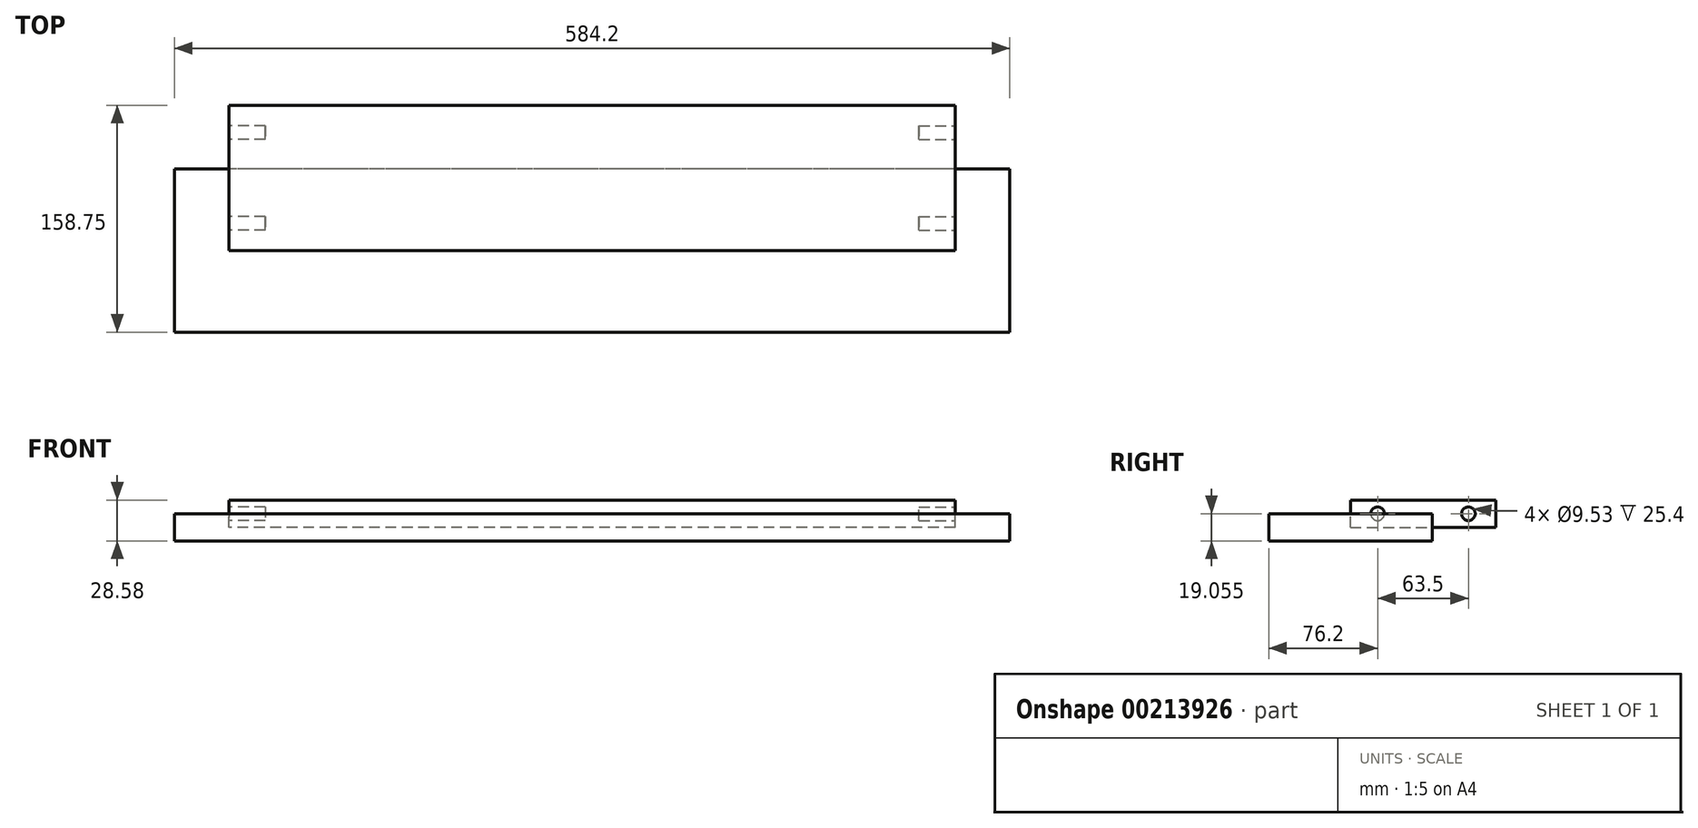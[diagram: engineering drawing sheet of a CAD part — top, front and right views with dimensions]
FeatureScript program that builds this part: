
annotation { "Feature Type Name" : "Feature", "Feature Type Description" : "" }
export const myFeature = defineFeature(function(context is Context, id is Id, definition is map)
    precondition{}
    {
        {
            var Q0;
            Q0=qCreatedBy(makeId("Right.planeOp"),FACE);
            var sketch = newSketch(context, id + "F0", { "sketchPlane" : qUnion([Q0])});
            skLineSegment(sketch, "E0.bottom", {"start": v(0, 0) * mm, "end": v(101.6, 0) * mm});
            skLineSegment(sketch, "E0.top", {"start": v(0, 19.05) * mm, "end": v(101.6, 19.05) * mm});
            skLineSegment(sketch, "E0.left", {"start": v(0, 0) * mm, "end": v(0, 19.05) * mm});
            skLineSegment(sketch, "E0.right", {"start": v(101.6, 0) * mm, "end": v(101.6, 19.05) * mm});
            skSolve(sketch);
        }
        {
            var Q0;
            Q0 = qSketchRegion(id + "F0", true);
            extrude(context, id + "F1", {"entities" : qUnion([Q0]), "endBound" : BoundingType.SYMMETRIC, "depth" : 508 * mm});
        }
        {
            var Q0;
            Q0=makeQuery(id+"F1.opExtrude","CAP_FACE",FACE,{"disambiguationData":[OSD([sQuery(id+"F0.wireOp",EDGE,"E0.bottom"),sQuery(id+"F0.wireOp",EDGE,"E0.top"),sQuery(id+"F0.wireOp",EDGE,"E0.left"),sQuery(id+"F0.wireOp",EDGE,"E0.right")])],"isStart":false});
            var sketch = newSketch(context, id + "F2", { "sketchPlane" : qUnion([Q0])});
            skCircle(sketch, "E1", {"center": v(19.05, 9.53) * mm, "radius": 4.76 * mm});
            skCircle(sketch, "E2.1.0.0", {"center": v(82.55, 9.53) * mm, "radius": 4.76 * mm});
            skLineSegment(sketch, "E2.direction1", {"start": v(19.05, 9.53) * mm, "end": v(82.55, 9.53) * mm, "construction": true});
            skSolve(sketch);
        }
        {
            var Q0;
            Q0 = qSketchRegion(id + "F2", true);
            extrude(context, id + "F3", {"entities" : qUnion([Q0]), "operationType" : NewBodyOperationType.REMOVE, "oppositeDirection" : true, "depth" : 25.4 * mm});
        }
        {
            var Q0;
            Q0=makeQuery(id+"F1.opExtrude","CAP_FACE",FACE,{"disambiguationData":[OSD([sQuery(id+"F0.wireOp",EDGE,"E0.bottom"),sQuery(id+"F0.wireOp",EDGE,"E0.top"),sQuery(id+"F0.wireOp",EDGE,"E0.left"),sQuery(id+"F0.wireOp",EDGE,"E0.right")])],"isStart":true});
            var sketch = newSketch(context, id + "F4", { "sketchPlane" : qUnion([Q0])});
            skCircle(sketch, "E3", {"center": v(-82.55, 9.53) * mm, "radius": 4.76 * mm});
            skCircle(sketch, "E4.1.0.0", {"center": v(-19.05, 9.53) * mm, "radius": 4.76 * mm});
            skLineSegment(sketch, "E4.direction1", {"start": v(-82.55, 9.53) * mm, "end": v(-19.05, 9.53) * mm, "construction": true});
            skSolve(sketch);
        }
        {
            var Q0;
            Q0 = qSketchRegion(id + "F4", true);
            extrude(context, id + "F5", {"entities" : qUnion([Q0]), "operationType" : NewBodyOperationType.REMOVE, "oppositeDirection" : true, "depth" : 25.4 * mm});
        }
        {
            var Q0;
            Q0=qCreatedBy(makeId("Front.planeOp"),FACE);
            var sketch = newSketch(context, id + "F6", { "sketchPlane" : qUnion([Q0])});
            skLineSegment(sketch, "E5.bottom", {"start": v(292.1, 9.53) * mm, "end": v(-292.1, 9.53) * mm});
            skLineSegment(sketch, "E5.top", {"start": v(292.1, -9.53) * mm, "end": v(-292.1, -9.53) * mm});
            skLineSegment(sketch, "E5.left", {"start": v(292.1, 9.53) * mm, "end": v(292.1, -9.53) * mm});
            skLineSegment(sketch, "E5.right", {"start": v(-292.1, 9.53) * mm, "end": v(-292.1, -9.53) * mm});
            skPoint(sketch, "E5.middle", {"position": v(0, 0) * mm});
            skSolve(sketch);
        }
        {
            var Q0;
            Q0 = qSketchRegion(id + "F6", true);
            extrude(context, id + "F7", {"entities" : qUnion([Q0]), "endBound" : BoundingType.SYMMETRIC, "depth" : 114.3 * mm});
        }
    });
